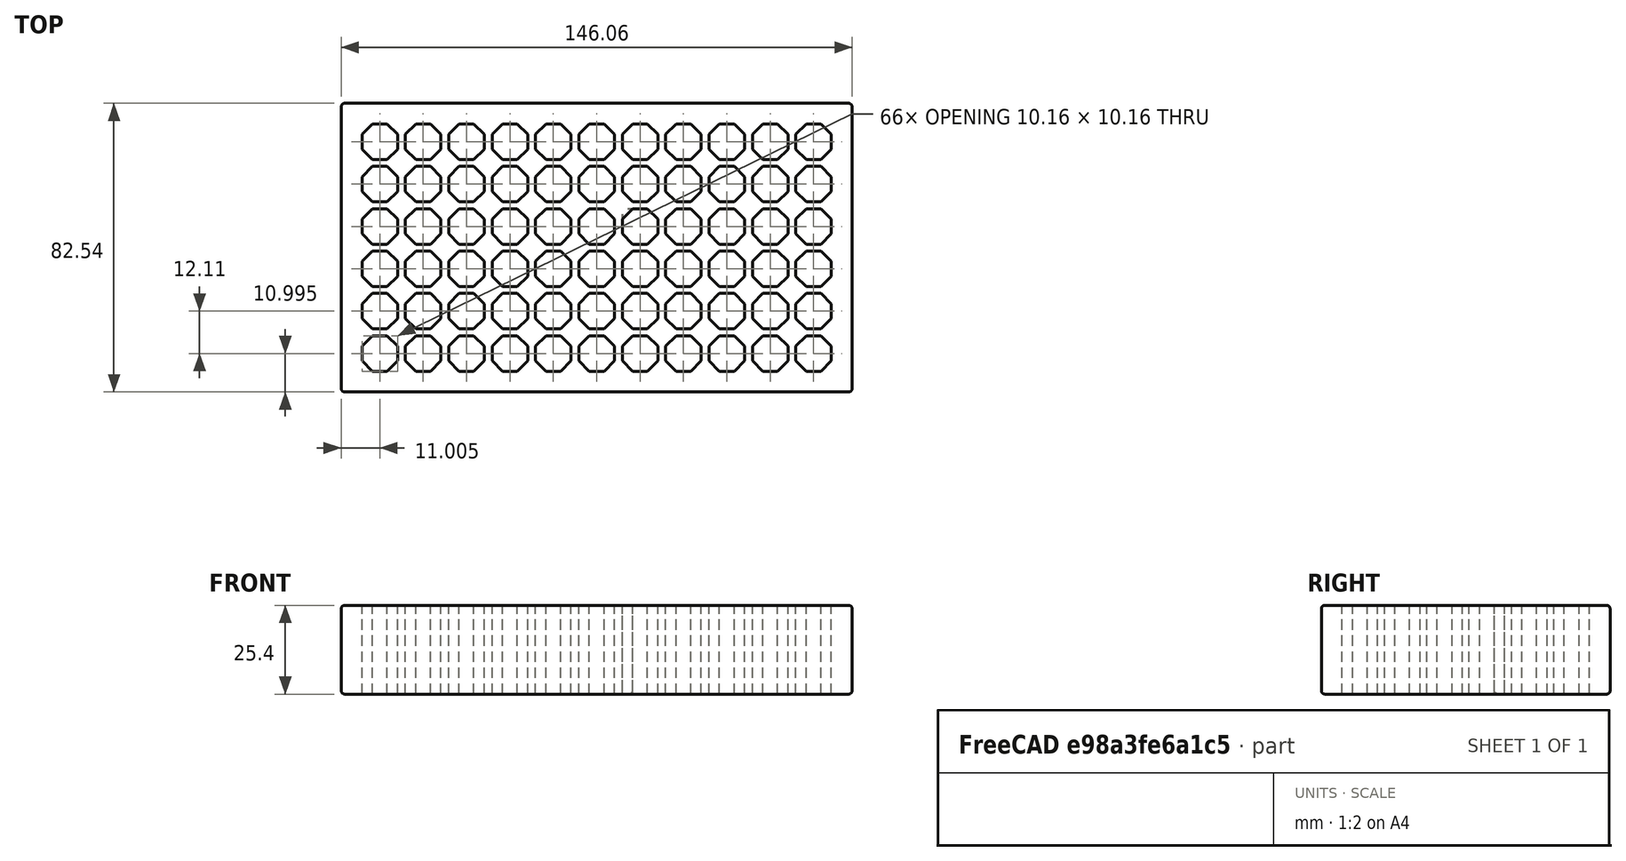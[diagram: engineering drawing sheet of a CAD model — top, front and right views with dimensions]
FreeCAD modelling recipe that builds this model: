
FCSTD DOCUMENT  (FreeCAD 0.21R33771 (Git))
Label: batt_spacer
License: All rights reserved
LicenseURL: http://en.wikipedia.org/wiki/All_rights_reserved
objects: Sketcher::SketchObject×2, PartDesign::LinearPattern×2, Spreadsheet::Sheet×1, PartDesign::Pad×1, PartDesign::Pocket×1, PartDesign::MultiTransform×1, PartDesign::Fillet×1, PartDesign::Body×1, App::Part×1, Mesh::Feature×1
note: 12 computed .brp shape members not serialized (recipe doc carries the construction recipe); baked Part::Feature solids carry a one-line shape summary decoded from their .brp

FEATURE [Spreadsheet::Sheet] Spreadsheet  label="Parameters"
  cells = A2='Length; B2=5.75; C2='inches; E2(length)==25.4 * B2; F2='mm; A3='Width; B3=3.25; C3='inches; E3(width)==25.4 * B3; F3='mm; A4='Height; B4=1; C4='inches; E4(height)==25.4 * B4; F4='mm; A5='Hole Diameter; B5(hole_diameter)=11; C5='mm
FEATURE [Sketcher::SketchObject] Sketch  label="Base-Sketch"
  FullyConstrained = true
  MapMode = 5
  Support = -> [XY_Plane001]
  expr: Constraints[10] = <<Parameters>>.width
  expr: Constraints[9] = <<Parameters>>.length
  sketch-geometry (4):
    g0: LineSegment StartX=-73.025 StartY=41.275 StartZ=0 EndX=73.025 EndY=41.275 EndZ=0
    g1: LineSegment StartX=73.025 StartY=41.275 StartZ=0 EndX=73.025 EndY=-41.275 EndZ=0
    g2: LineSegment StartX=73.025 StartY=-41.275 StartZ=0 EndX=-73.025 EndY=-41.275 EndZ=0
    g3: LineSegment StartX=-73.025 StartY=-41.275 StartZ=0 EndX=-73.025 EndY=41.275 EndZ=0
  constraints (11):
    c: Coincident(g0,g1)
    c: Coincident(g1,g2)
    c: Coincident(g2,g3)
    c: Coincident(g3,g0)
    c: Horizontal(g0)
    c: Horizontal(g2)
    c: Vertical(g1)
    c: Vertical(g3)
    c: Symmetric(g2,g0,g-1)
    c: DistanceX(g0,g0) = 146.05
    c: DistanceY(g1,g1) = 82.55
FEATURE [PartDesign::Pad] Pad
  Direction = (0,0,1)
  Length = 25.4
  Length2 = 10
  Profile = -> Sketch
  ReferenceAxis = -> Sketch [N_Axis]
  Type = 0
  expr: Length = <<Parameters>>.height
FEATURE [Sketcher::SketchObject] Sketch001  label="Hole-Sketch"
  FullyConstrained = true
  MapMode = 5
  Support = -> [XY_Plane001]
  expr: Constraints[23] = <<Parameters>>.hole_diameter
  expr: Constraints[24] = <<Parameters>>.width / 2 - <<Parameters>>.hole_diameter
  expr: Constraints[25] = <<Parameters>>.length / 2 - <<Parameters>>.hole_diameter
  sketch-geometry (9):
    g0: LineSegment StartX=-59.9202 StartY=25.1937 StartZ=0 EndX=-56.9437 EndY=28.1702 EndZ=0
    g1: LineSegment StartX=-56.9437 StartY=28.1702 StartZ=0 EndX=-56.9437 EndY=32.3798 EndZ=0
    g2: LineSegment StartX=-56.9437 StartY=32.3798 StartZ=0 EndX=-59.9202 EndY=35.3563 EndZ=0
    g3: LineSegment StartX=-59.9202 StartY=35.3563 StartZ=0 EndX=-64.1298 EndY=35.3563 EndZ=0
    g4: LineSegment StartX=-64.1298 StartY=35.3563 StartZ=0 EndX=-67.1063 EndY=32.3798 EndZ=0
    g5: LineSegment StartX=-67.1063 StartY=32.3798 StartZ=0 EndX=-67.1063 EndY=28.1702 EndZ=0
    g6: LineSegment StartX=-67.1063 StartY=28.1702 StartZ=0 EndX=-64.1298 EndY=25.1937 EndZ=0
    g7: LineSegment StartX=-64.1298 StartY=25.1937 StartZ=0 EndX=-59.9202 EndY=25.1937 EndZ=0
    g8: Circle CenterX=-62.025 CenterY=30.275 CenterZ=0 NormalX=0 NormalY=0 NormalZ=1 AngleXU=0 Radius=5.5
  constraints (21):
    c: Coincident(g0,g1)
    c: Coincident(g1,g2)
    c: Coincident(g2,g3)
    c: Coincident(g3,g4)
    c: Coincident(g4,g5)
    c: Coincident(g5,g6)
    c: Coincident(g6,g7)
    c: Coincident(g7,g0)
    c: Equal(g0, g1-g7) x7
    c: PointOnObject(g0,g8)
    c: PointOnObject(g1,g8)
    c: PointOnObject(g2,g8)
    c: PointOnObject(g3,g8)
    c: PointOnObject(g4,g8)
    c: PointOnObject(g5,g8)
    c: PointOnObject(g6,g8)
    c: PointOnObject(g7,g8)
    c: Diameter(g8) = 11
    c: DistanceY(g-1,g8) = 30.275
    c: DistanceX(g8,g-1) = 62.025
    c: Horizontal(g3)
FEATURE [PartDesign::Pocket] Pocket
  BaseFeature = -> Pad
  Direction = (0,0,-1)
  Length = 38.1
  Length2 = 5
  Profile = -> Sketch001
  ReferenceAxis = -> Sketch001 [N_Axis]
  Reversed = true
  Type = 0
  expr: Length = <<Parameters>>.height * 1.5
FEATURE [PartDesign::LinearPattern] LinearPattern
  Direction = -> Sketch001 [H_Axis]
  Length = 124.05
  Occurrences = 11
  expr: Length = <<Parameters>>.length - 2 * <<Parameters>>.hole_diameter
FEATURE [PartDesign::LinearPattern] LinearPattern001
  Direction = -> Sketch001 [V_Axis]
  Length = 60.55
  Occurrences = 6
  Reversed = true
  expr: Length = <<Parameters>>.width - 2 * <<Parameters>>.hole_diameter
FEATURE [PartDesign::MultiTransform] MultiTransform
  BaseFeature = -> Pocket
  Originals = -> [Pocket]
  Transformations = -> [LinearPattern,LinearPattern001]
FEATURE [PartDesign::Fillet] Fillet
  Base = -> MultiTransform [Edge408,Edge7,Edge4,Edge10,Edge8,Edge9,Edge11,Edge2,Edge3,Edge1,Edge6,Edge5,Edge540]
  BaseFeature = -> MultiTransform
  Radius = 1
  SupportTransform = false
  UseAllEdges = false
FEATURE [PartDesign::Body] Body
  Group = -> [Sketch,Pad,Sketch001,Pocket,MultiTransform,LinearPattern,LinearPattern001,Fillet]
  Origin = -> Origin001
  Tip = -> Fillet
FEATURE [App::Part] Part
  Group = -> [Body]
  Origin = -> Origin
FEATURE [Mesh::Feature] Mesh  label="Fillet (Meshed)"
